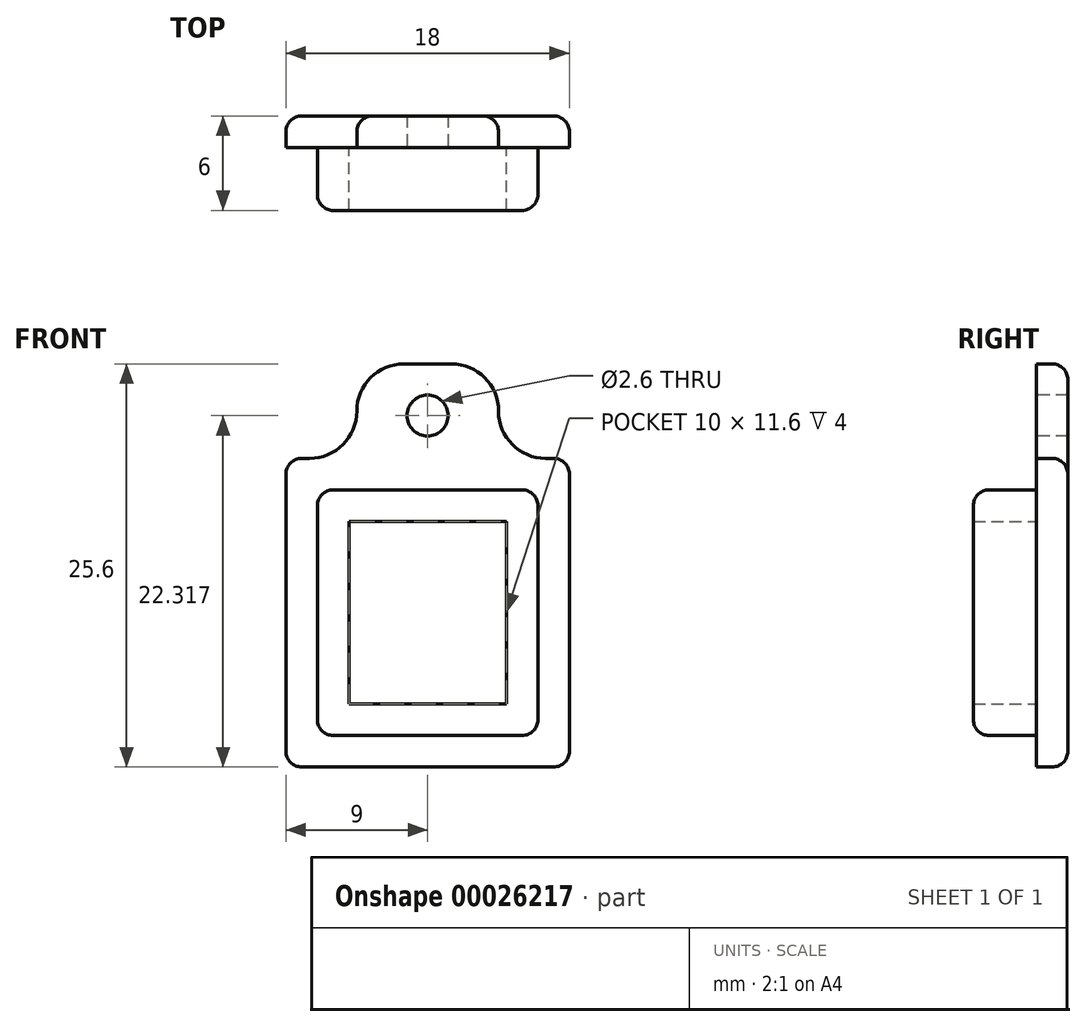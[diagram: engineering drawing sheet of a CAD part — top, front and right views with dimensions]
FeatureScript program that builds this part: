
annotation { "Feature Type Name" : "Feature", "Feature Type Description" : "" }
export const myFeature = defineFeature(function(context is Context, id is Id, definition is map)
    precondition{}
    {
        {
            var Q0;
            Q0=qCreatedBy(makeId("Front.planeOp"),FACE);
            var sketch = newSketch(context, id + "F0", { "sketchPlane" : qUnion([Q0])});
            skLineSegment(sketch, "E0.rect.bottom", {"start": v(7, -7.8) * mm, "end": v(-7, -7.8) * mm});
            skLineSegment(sketch, "E0.rect.top", {"start": v(7, 7.8) * mm, "end": v(-7, 7.8) * mm});
            skLineSegment(sketch, "E0.rect.left", {"start": v(7, -7.8) * mm, "end": v(7, 7.8) * mm});
            skLineSegment(sketch, "E0.rect.right", {"start": v(-7, -7.8) * mm, "end": v(-7, 7.8) * mm});
            skPoint(sketch, "E0.rect.middle", {"position": v(0, 0) * mm});
            skLineSegment(sketch, "E1.0", {"start": v(9, 9.8) * mm, "end": v(7.5, 9.8) * mm});
            skLineSegment(sketch, "E1.1", {"start": v(9, -9.8) * mm, "end": v(9, 9.8) * mm});
            skLineSegment(sketch, "E1.2", {"start": v(9, -9.8) * mm, "end": v(-9, -9.8) * mm});
            skLineSegment(sketch, "E1.3", {"start": v(-9, -9.8) * mm, "end": v(-9, 9.8) * mm});
            skLineSegment(sketch, "E2.bottom", {"start": v(-1.5, 15.8) * mm, "end": v(1.5, 15.8) * mm});
            skLineSegment(sketch, "E2.top", {"start": v(-4.5, 9.8) * mm, "end": v(4.5, 9.8) * mm});
            skLineSegment(sketch, "E2.left", {"start": v(-4.5, 12.8) * mm, "end": v(-4.5, 12.8) * mm});
            skLineSegment(sketch, "E2.right", {"start": v(4.5, 12.8) * mm, "end": v(4.5, 12.8) * mm});
            skCircle(sketch, "E3", {"center": v(0, 12.52) * mm, "radius": 1.3 * mm});
            skPoint(sketch, "E4.visualSharp", {"position": v(-4.5, 15.8) * mm});
            skArc(sketch, "E4.filletArc", {"start": v(-1.5, 15.8) * mm, "mid": v(-3.62, 14.92) * mm, "end": v(-4.5, 12.8) * mm});
            skPoint(sketch, "E5.visualSharp", {"position": v(4.5, 15.8) * mm});
            skArc(sketch, "E5.filletArc", {"start": v(4.5, 12.8) * mm, "mid": v(3.62, 14.92) * mm, "end": v(1.5, 15.8) * mm});
            skPoint(sketch, "E6.newPointA", {"position": v(4.5, 9.8) * mm});
            skArc(sketch, "E6.filletArc", {"start": v(4.5, 12.8) * mm, "mid": v(5.38, 10.68) * mm, "end": v(7.5, 9.8) * mm});
            skLineSegment(sketch, "E7", {"start": v(-9, 9.8) * mm, "end": v(-7.5, 9.8) * mm});
            skPoint(sketch, "E8.visualSharp", {"position": v(-4.5, 9.8) * mm});
            skArc(sketch, "E8.filletArc", {"start": v(-7.5, 9.8) * mm, "mid": v(-5.38, 10.68) * mm, "end": v(-4.5, 12.8) * mm});
            skSolve(sketch);
        }
        {
            var Q0;
            Q0=makeQuery(id+"F0.imprint","IMPRINT",FACE,{"disambiguationData":[TD([[makeQuery(id+"F0.imprint","IMPRINT",EDGE,{"derivedFrom":sQuery(id+"F0.wireOp",EDGE,"E0.rect.bottom")}),-1.0]])]});
            extrude(context, id + "F1", {"entities" : qUnion([Q0]), "depth" : 4 * mm});
        }
        {
            var Q0;
            Q0=makeQuery(id+"F0.imprint","IMPRINT",FACE,{"disambiguationData":[TD([[makeQuery(id+"F0.imprint","IMPRINT",EDGE,{"derivedFrom":sQuery(id+"F0.wireOp",EDGE,"E0.rect.bottom")}),1.0]])]});
            var Q1;
            Q1=makeQuery(id+"F0.imprint","IMPRINT",FACE,{"disambiguationData":[TD([[makeQuery(id+"F0.imprint","IMPRINT",EDGE,{"derivedFrom":sQuery(id+"F0.wireOp",EDGE,"E0.rect.bottom")}),-1.0]])]});
            var Q2;
            Q2=makeQuery(id+"F0.imprint","IMPRINT",FACE,{"disambiguationData":[TD([[makeQuery(id+"F0.imprint","IMPRINT",EDGE,{"derivedFrom":sQuery(id+"F0.wireOp",EDGE,"E2.bottom")}),-1.0]])]});
            extrude(context, id + "F2", {"entities" : qUnion([Q0, Q1, Q2]), "operationType" : NewBodyOperationType.ADD, "oppositeDirection" : true, "depth" : 2 * mm});
        }
        {
            var Q0;
            Q0=makeQuery(id+"F1.opExtrude","SWEPT_EDGE",EDGE,{"disambiguationData":[OSD([sQuery(id+"F0.wireOp",EDGE,"E0.rect.top"),sQuery(id+"F0.wireOp",EDGE,"E0.rect.left")])]});
            var Q1;
            Q1=makeQuery(id+"F1.opExtrude","SWEPT_EDGE",EDGE,{"disambiguationData":[OSD([sQuery(id+"F0.wireOp",EDGE,"E0.rect.top"),sQuery(id+"F0.wireOp",EDGE,"E0.rect.right")])]});
            var Q2;
            Q2=makeQuery(id+"F1.opExtrude","SWEPT_EDGE",EDGE,{"disambiguationData":[OSD([sQuery(id+"F0.wireOp",EDGE,"E0.rect.bottom"),sQuery(id+"F0.wireOp",EDGE,"E0.rect.right")])]});
            var Q3;
            Q3=makeQuery(id+"F1.opExtrude","SWEPT_EDGE",EDGE,{"disambiguationData":[OSD([sQuery(id+"F0.wireOp",EDGE,"E0.rect.bottom"),sQuery(id+"F0.wireOp",EDGE,"E0.rect.left")])]});
            var Q4;
            Q4=makeQuery(id+"F1.opExtrude","CAP_FACE",FACE,{"disambiguationData":[OSD([sQuery(id+"F0.wireOp",EDGE,"E0.rect.bottom"),sQuery(id+"F0.wireOp",EDGE,"E0.rect.top"),sQuery(id+"F0.wireOp",EDGE,"E0.rect.left"),sQuery(id+"F0.wireOp",EDGE,"E0.rect.right")])],"isStart":false});
            var Q5;
            Q5=makeQuery(id+"F2.opExtrude","SWEPT_EDGE",EDGE,{"disambiguationData":[OSD([sQuery(id+"F0.wireOp",EDGE,"E1.0"),sQuery(id+"F0.wireOp",EDGE,"E1.1")])]});
            var Q6;
            Q6=makeQuery(id+"F2.opExtrude","SWEPT_EDGE",EDGE,{"disambiguationData":[OSD([sQuery(id+"F0.wireOp",EDGE,"E1.0"),sQuery(id+"F0.wireOp",EDGE,"E2.top"),sQuery(id+"F0.wireOp",EDGE,"E2.right")])]});
            var Q7;
            Q7=makeQuery(id+"F2.opExtrude","SWEPT_EDGE",EDGE,{"disambiguationData":[OSD([sQuery(id+"F0.wireOp",EDGE,"E2.bottom"),sQuery(id+"F0.wireOp",EDGE,"E2.right")])]});
            var Q8;
            Q8=makeQuery(id+"F2.opExtrude","SWEPT_EDGE",EDGE,{"disambiguationData":[OSD([sQuery(id+"F0.wireOp",EDGE,"E2.bottom"),sQuery(id+"F0.wireOp",EDGE,"E2.left")])]});
            var Q9;
            Q9=makeQuery(id+"F2.opExtrude","SWEPT_EDGE",EDGE,{"disambiguationData":[OSD([sQuery(id+"F0.wireOp",EDGE,"E1.0"),sQuery(id+"F0.wireOp",EDGE,"E2.top"),sQuery(id+"F0.wireOp",EDGE,"E2.left")])]});
            var Q10;
            Q10=makeQuery(id+"F2.opExtrude","SWEPT_EDGE",EDGE,{"disambiguationData":[OSD([sQuery(id+"F0.wireOp",EDGE,"E1.0"),sQuery(id+"F0.wireOp",EDGE,"E1.3")])]});
            var Q11;
            Q11=makeQuery(id+"F2.opExtrude","SWEPT_EDGE",EDGE,{"disambiguationData":[OSD([sQuery(id+"F0.wireOp",EDGE,"E1.1"),sQuery(id+"F0.wireOp",EDGE,"E1.2")])]});
            var Q12;
            Q12=makeQuery(id+"F2.opExtrude","SWEPT_EDGE",EDGE,{"disambiguationData":[OSD([sQuery(id+"F0.wireOp",EDGE,"E1.2"),sQuery(id+"F0.wireOp",EDGE,"E1.3")])]});
            var Q13;
            Q13=makeQuery(id+"F2.opExtrude","CAP_EDGE",EDGE,{"disambiguationData":[OSD([sQuery(id+"F0.wireOp",EDGE,"E1.1")])],"isStart":false});
            var Q14;
            Q14=makeQuery(id+"F2.opExtrude","CAP_EDGE",EDGE,{"disambiguationData":[OSD([sQuery(id+"F0.wireOp",EDGE,"E1.2")])],"isStart":false});
            var Q15;
            Q15=makeQuery(id+"F2.opExtrude","CAP_EDGE",EDGE,{"disambiguationData":[OSD([sQuery(id+"F0.wireOp",EDGE,"E1.3")])],"isStart":false});
            var Q16;
            {var subQ0=sQuery(id+"F0.wireOp",EDGE,"E1.0");Q16=makeQuery(id+"F2.opExtrude","CAP_EDGE",EDGE,{"disambiguationData":[OSD([subQ0]),TDD([makeQuery(id+"F0.imprint","IMPRINT",EDGE,{"disambiguationData":[TD([[makeQuery(id+"F0.imprint","INTERSECT",VERTEX,{"derivedFrom":[subQ0,sQuery(id+"F0.wireOp",EDGE,"E1.3")]}),1.0]])],"derivedFrom":subQ0})])],"isStart":false});}
            var Q17;
            Q17=makeQuery(id+"F2.opExtrude","CAP_EDGE",EDGE,{"disambiguationData":[OSD([sQuery(id+"F0.wireOp",EDGE,"E2.bottom")])],"isStart":false});
            var Q18;
            Q18=makeQuery(id+"F2.opExtrude","CAP_EDGE",EDGE,{"disambiguationData":[OSD([sQuery(id+"F0.wireOp",EDGE,"E2.right")])],"isStart":false});
            fillet(context, id + "F3", {"entities" : qUnion([Q0, Q1, Q2, Q3, Q4, Q5, Q6, Q7, Q8, Q9, Q10, Q11, Q12, Q13, Q14, Q15, Q16, Q17, Q18]), "radius" : 1 * mm, "tangentPropagation" : true, "allowEdgeOverflow" : false});
        }
        {
            var Q0;
            Q0=makeQuery(id+"F1.opExtrude","CAP_FACE",FACE,{"disambiguationData":[OSD([sQuery(id+"F0.wireOp",EDGE,"E0.rect.bottom"),sQuery(id+"F0.wireOp",EDGE,"E0.rect.top"),sQuery(id+"F0.wireOp",EDGE,"E0.rect.left"),sQuery(id+"F0.wireOp",EDGE,"E0.rect.right")])],"isStart":false});
            shell(context, id + "F4", {"entities" : qUnion([Q0]), "thickness" : 2 * mm});
        }
    });
